# Revit family: 293 BFS-BGU-DSD-ME-___ (LOD400)
name_source: partatom
category: Fire Alarm Devices
revit_build: Autodesk Revit 2018 (Build: 20170223_1515(x64)
units: mm (PartAtom-declared; Revit-internal decimal feet)

## family parameters
Cut with Voids When Loaded = No
Host = Face
Maintain Annotation Orientation = No
OmniClass Number = 23.29.31.17.11
OmniClass Title = Visible Fire Notification Device Lights
Part Type = Normal
Room Calculation Point = No
Round Connector Dimension = Use Diameter
Shared = No

## types (1)
- BFS-BGU-DSD-ME-___
    2D Symbol_DI_Scale = DI_BFB_BGU : 1 To 50
    DSD.BFS.Height = 0 mm  [stored 0 ft]
    DSD.BFS.Length = 0 mm  [stored 0 ft]
    DSD.BFS.Width = 0 mm  [stored 0 ft]
    Default Elevation = 0 mm  [stored 0 ft]
    Glass Plane = GL_Blue_128-255-255
    Height = 56 mm  [stored 0.183727 ft]
    Inner Material = PL_White_255-255-255
    Length = 87 mm  [stored 0.285433 ft]
    Main Material = PL_Red_198-000-000
    Radius = 22 mm
    Text Color = PL_Black_000-000-000
    Width = 87 mm  [stored 0.285433 ft]

note: [stored X ft] marks values corroborated as IEEE doubles in the binary element streams (Revit-internal decimal feet)

## geometry (parser evidence)
native form markers: Blend x2, Sweep x5
no freeform markers — native parametric forms only
